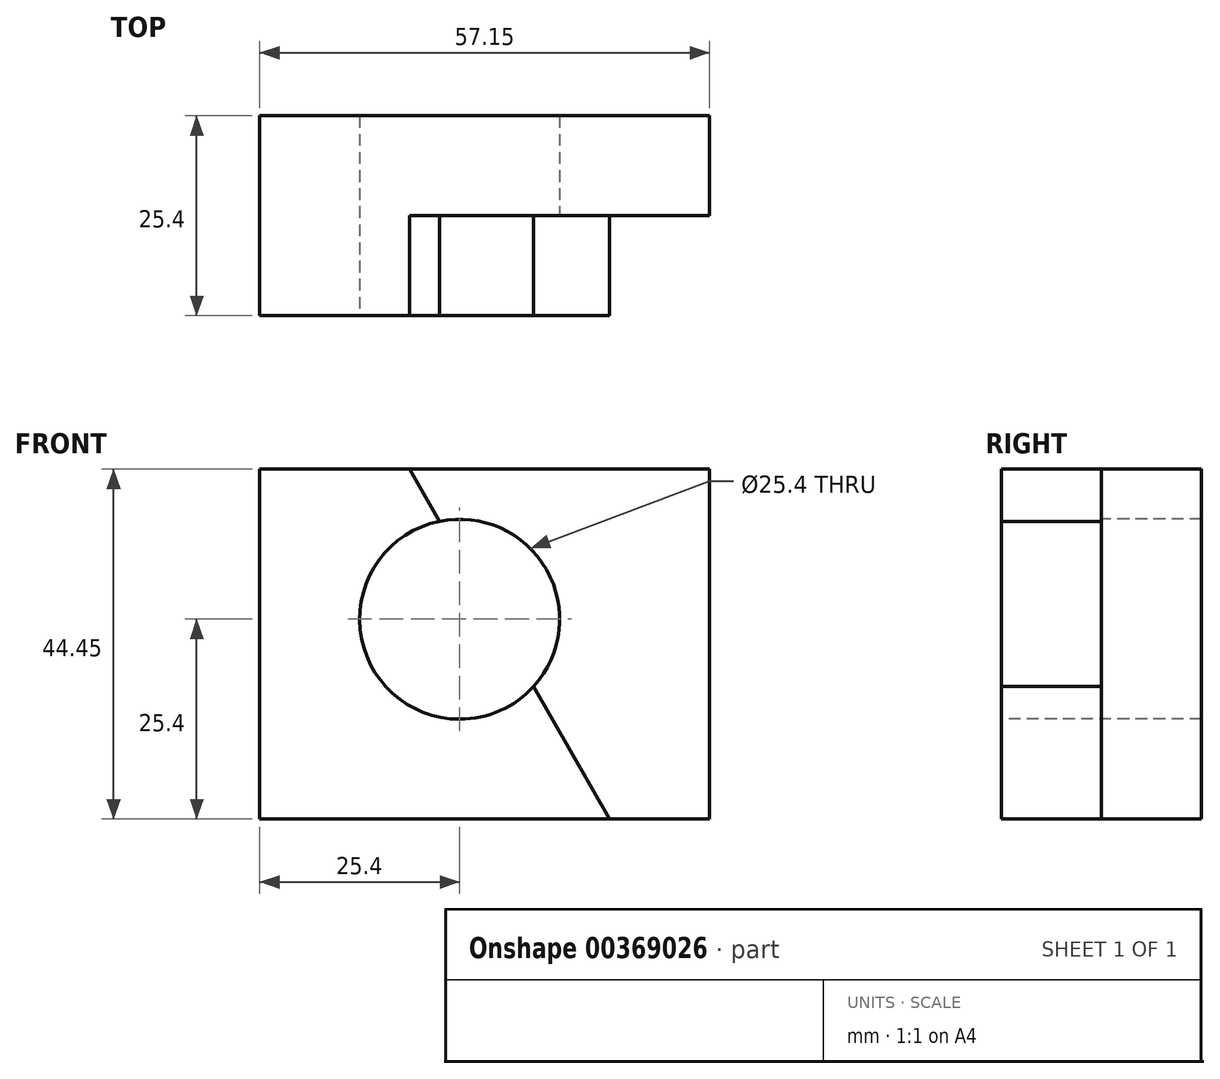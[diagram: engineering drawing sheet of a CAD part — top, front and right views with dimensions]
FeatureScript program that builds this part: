
annotation { "Feature Type Name" : "Feature", "Feature Type Description" : "" }
export const myFeature = defineFeature(function(context is Context, id is Id, definition is map)
    precondition{}
    {
        {
            var Q0;
            Q0=qCreatedBy(makeId("Front.planeOp"),FACE);
            var sketch = newSketch(context, id + "F0", { "sketchPlane" : qUnion([Q0])});
            skLineSegment(sketch, "E0", {"start": v(0, 0) * mm, "end": v(0, 44.45) * mm});
            skLineSegment(sketch, "E1", {"start": v(0, 44.45) * mm, "end": v(19.05, 44.45) * mm});
            skLineSegment(sketch, "E2", {"start": v(19.05, 44.45) * mm, "end": v(57.15, 44.45) * mm});
            skLineSegment(sketch, "E3", {"start": v(57.15, 44.45) * mm, "end": v(57.15, 0) * mm});
            skLineSegment(sketch, "E4", {"start": v(57.15, 0) * mm, "end": v(44.45, 0) * mm});
            skLineSegment(sketch, "E5", {"start": v(0, 0) * mm, "end": v(44.45, 0) * mm});
            skLineSegment(sketch, "E6", {"start": v(44.45, 0) * mm, "end": v(19.05, 44.45) * mm});
            skSolve(sketch);
        }
        {
            var Q0;
            Q0=makeQuery(id+"F0.imprint","IMPRINT",FACE,{"disambiguationData":[TD([[makeQuery(id+"F0.imprint","IMPRINT",EDGE,{"derivedFrom":sQuery(id+"F0.wireOp",EDGE,"E2")}),-1.0]])]});
            extrude(context, id + "F1", {"entities" : qUnion([Q0]), "depth" : 12.7 * mm});
        }
        {
            var Q0;
            Q0=makeQuery(id+"F0.imprint","IMPRINT",FACE,{"disambiguationData":[TD([[makeQuery(id+"F0.imprint","IMPRINT",EDGE,{"derivedFrom":sQuery(id+"F0.wireOp",EDGE,"E0")}),-1.0]])]});
            extrude(context, id + "F2", {"entities" : qUnion([Q0]), "operationType" : NewBodyOperationType.ADD, "depth" : 25.4 * mm});
        }
        {
            var Q0;
            Q0=makeQuery(id+"F2.opExtrude","CAP_FACE",FACE,{"disambiguationData":[OSD([sQuery(id+"F0.wireOp",EDGE,"E0"),sQuery(id+"F0.wireOp",EDGE,"E1"),sQuery(id+"F0.wireOp",EDGE,"E5"),sQuery(id+"F0.wireOp",EDGE,"E6")])],"isStart":false});
            var sketch = newSketch(context, id + "F3", { "sketchPlane" : qUnion([Q0])});
            skLineSegment(sketch, "E7", {"start": v(0, 0) * mm, "end": v(0, 25.4) * mm});
            skLineSegment(sketch, "E8", {"start": v(0, 25.4) * mm, "end": v(25.4, 25.4) * mm});
            skCircle(sketch, "E9", {"center": v(25.4, 25.4) * mm, "radius": 12.7 * mm});
            skSolve(sketch);
        }
        {
            var Q0;
            {var subQ0=sQuery(id+"F3.wireOp",EDGE,"E9");var subQ1=makeQuery(id+"F2.opExtrude","CAP_EDGE",EDGE,{"disambiguationData":[OSD([sQuery(id+"F0.wireOp",EDGE,"E6")])],"isStart":false});var subQ2=makeQuery(id+"F3.imprint","INTERSECT",VERTEX,{"disambiguationData":[OD(0.0)],"derivedFrom":[subQ1,subQ0]});Q0=makeQuery(id+"F3.imprint","IMPRINT",FACE,{"disambiguationData":[TD([[makeQuery(id+"F3.imprint","IMPRINT",EDGE,{"disambiguationData":[TD([[subQ2,1.0]])],"derivedFrom":subQ0}),1.0]])]});}
            var Q1;
            {var subQ0=sQuery(id+"F3.wireOp",EDGE,"E9");var subQ1=makeQuery(id+"F3.imprint","INTERSECT",VERTEX,{"derivedFrom":[sQuery(id+"F3.wireOp",EDGE,"E8"),subQ0]});Q1=makeQuery(id+"F3.imprint","IMPRINT",FACE,{"disambiguationData":[TD([[makeQuery(id+"F3.imprint","IMPRINT",EDGE,{"disambiguationData":[TD([[subQ1,1.0]])],"derivedFrom":subQ0}),1.0]])]});}
            var Q2;
            Q2=sQuery(id+"F3.wireOp",EDGE,"E9");
            extrude(context, id + "F4", {"entities" : qUnion([Q0, Q1]), "operationType" : NewBodyOperationType.REMOVE, "surfaceEntities" : qUnion([Q2]), "oppositeDirection" : true, "depth" : 50.8 * mm});
        }
    });
